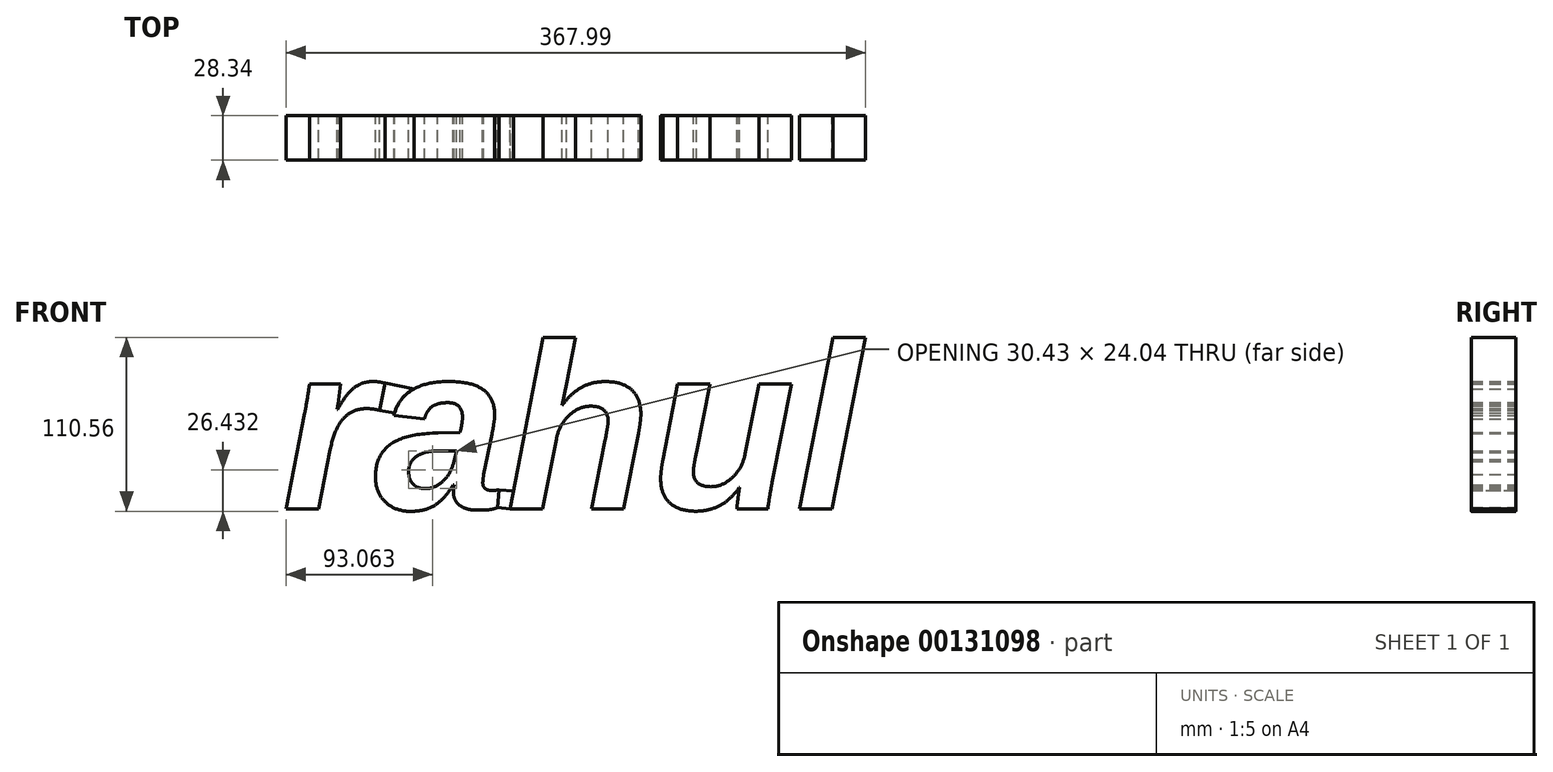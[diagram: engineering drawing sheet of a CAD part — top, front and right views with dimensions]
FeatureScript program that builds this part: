
annotation { "Feature Type Name" : "Feature", "Feature Type Description" : "" }
export const myFeature = defineFeature(function(context is Context, id is Id, definition is map)
    precondition{}
    {
        {
            var Q0;
            Q0=qCreatedBy(makeId("Front.planeOp"),FACE);
            var sketch = newSketch(context, id + "F0", { "sketchPlane" : qUnion([Q0])});
            skText(sketch, "E0", { "text": "rahul", "fontName": "Arimo-BoldItalic.ttf"});
            const initialGuessF0  = {"E0": [-0.2436, 0, 1, 0, 0.10837]};
            skSetInitialGuess(sketch, initialGuessF0);
            skSolve(sketch);
        }
        {
            var Q0;
            Q0 = qSketchRegion(id + "F0", true);
            extrude(context, id + "F1", {"entities" : qUnion([Q0]), "depth" : 28.34 * mm});
        }
        {
            var Q0;
            Q0=makeQuery(id+"F1.opExtrude","SWEPT_FACE",FACE,{"disambiguationData":[OSD([sQuery(id+"F0.wireOp",EDGE,"E0.sketch_text.stroke-14")])]});
            extrude(context, id + "F2", {"entities" : qUnion([Q0]), "endBound" : BoundingType.UP_TO_NEXT, "depth" : 25.4 * mm});
        }
        {
            var Q0;
            Q0=makeQuery(id+"F1.opExtrude","SWEPT_FACE",FACE,{"disambiguationData":[OSD([sQuery(id+"F0.wireOp",EDGE,"E0.sketch_text.stroke-43")])]});
            extrude(context, id + "F3", {"entities" : qUnion([Q0]), "endBound" : BoundingType.UP_TO_NEXT, "depth" : 25.4 * mm});
        }
    });
